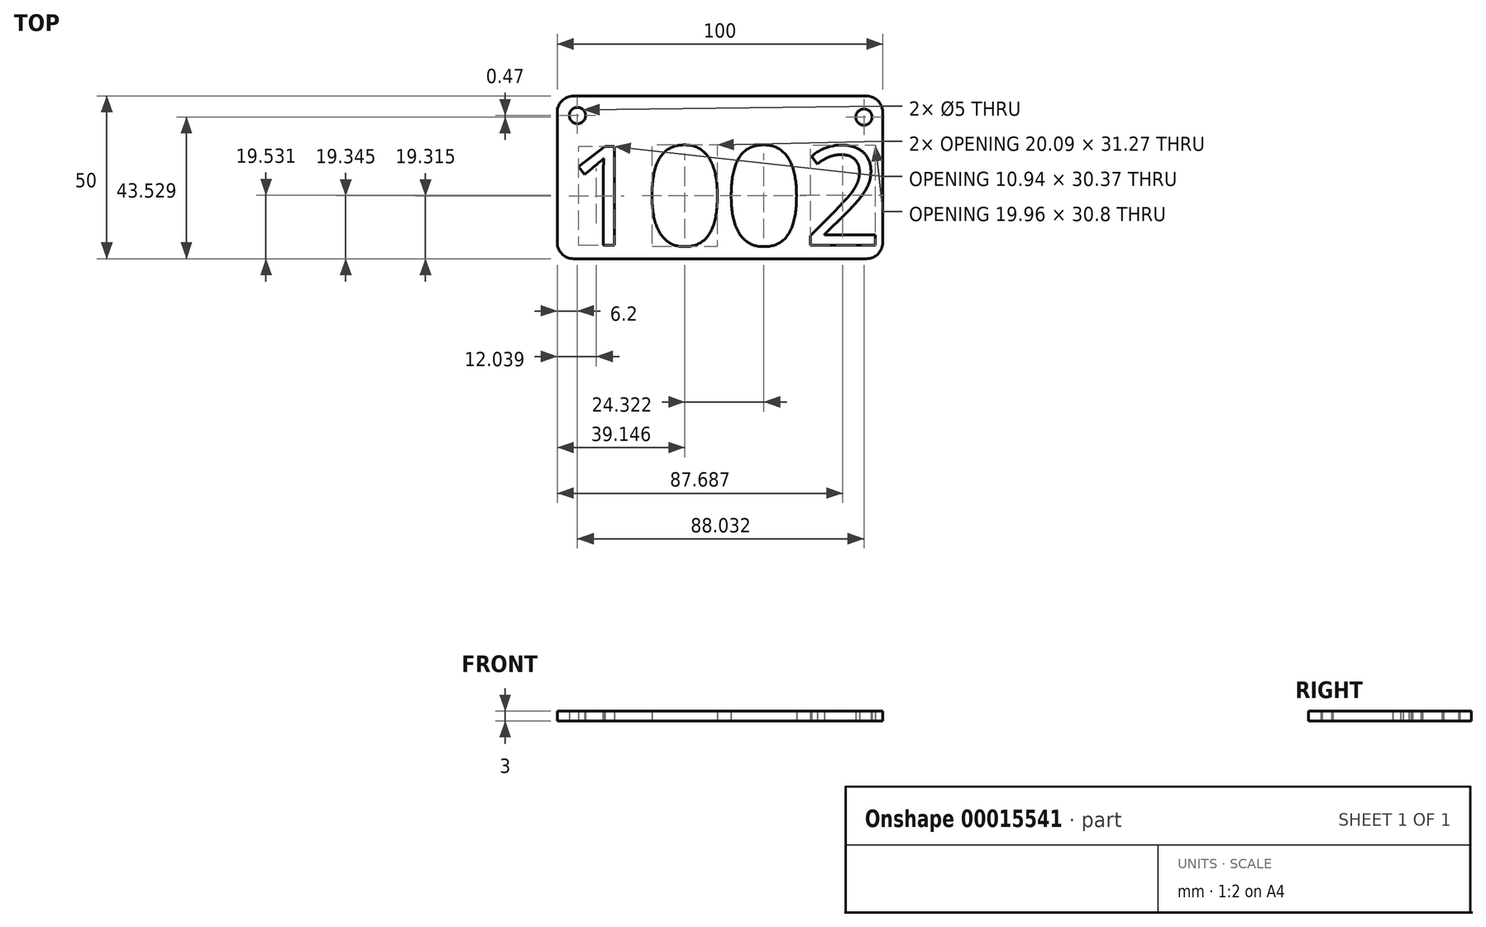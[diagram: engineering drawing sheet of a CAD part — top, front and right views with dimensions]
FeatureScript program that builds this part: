
annotation { "Feature Type Name" : "Feature", "Feature Type Description" : "" }
export const myFeature = defineFeature(function(context is Context, id is Id, definition is map)
    precondition{}
    {
        {
            var Q0;
            Q0=qCreatedBy(makeId("Top.planeOp"),FACE);
            var sketch = newSketch(context, id + "F0", { "sketchPlane" : qUnion([Q0])});
            skLineSegment(sketch, "E0.bottom", {"start": v(0, 0) * mm, "end": v(-100, 0) * mm});
            skLineSegment(sketch, "E0.top", {"start": v(0, 50) * mm, "end": v(-100, 50) * mm});
            skLineSegment(sketch, "E0.left", {"start": v(0, 0) * mm, "end": v(0, 50) * mm});
            skLineSegment(sketch, "E0.right", {"start": v(-100, 0) * mm, "end": v(-100, 50) * mm});
            skCircle(sketch, "E1", {"center": v(-93.8, 44) * mm, "radius": 2.5 * mm});
            skCircle(sketch, "E2", {"center": v(-5.77, 43.53) * mm, "radius": 2.5 * mm});
            skText(sketch, "E3", { "text": "1002", "fontName": "OpenSans-Regular.ttf"});
            const initialGuessF0  = {"E3": [-0.09734, 0.00413, 1, 0, 0.03063]};
            skSetInitialGuess(sketch, initialGuessF0);
            skSolve(sketch);
        }
        {
            var Q0;
            Q0=makeQuery(id+"F0.imprint","IMPRINT",FACE,{"disambiguationData":[TD([[makeQuery(id+"F0.imprint","IMPRINT",EDGE,{"derivedFrom":sQuery(id+"F0.wireOp",EDGE,"E0.bottom")}),-1.0]])]});
            extrude(context, id + "F1", {"entities" : qUnion([Q0]), "depth" : 3 * mm});
        }
        {
            var Q0;
            Q0=makeQuery(id+"F1.opExtrude","SWEPT_EDGE",EDGE,{"disambiguationData":[OSD([sQuery(id+"F0.wireOp",EDGE,"E0.top"),sQuery(id+"F0.wireOp",EDGE,"E0.right")])]});
            var Q1;
            Q1=makeQuery(id+"F1.opExtrude","SWEPT_EDGE",EDGE,{"disambiguationData":[OSD([sQuery(id+"F0.wireOp",EDGE,"E0.top"),sQuery(id+"F0.wireOp",EDGE,"E0.left")])]});
            var Q2;
            Q2=makeQuery(id+"F1.opExtrude","SWEPT_EDGE",EDGE,{"disambiguationData":[OSD([sQuery(id+"F0.wireOp",EDGE,"E0.bottom"),sQuery(id+"F0.wireOp",EDGE,"E0.left")])]});
            var Q3;
            Q3=makeQuery(id+"F1.opExtrude","SWEPT_EDGE",EDGE,{"disambiguationData":[OSD([sQuery(id+"F0.wireOp",EDGE,"E0.bottom"),sQuery(id+"F0.wireOp",EDGE,"E0.right")])]});
            fillet(context, id + "F2", {"entities" : qUnion([Q0, Q1, Q2, Q3]), "radius" : 5 * mm, "tangentPropagation" : true, "allowEdgeOverflow" : false});
        }
    });
